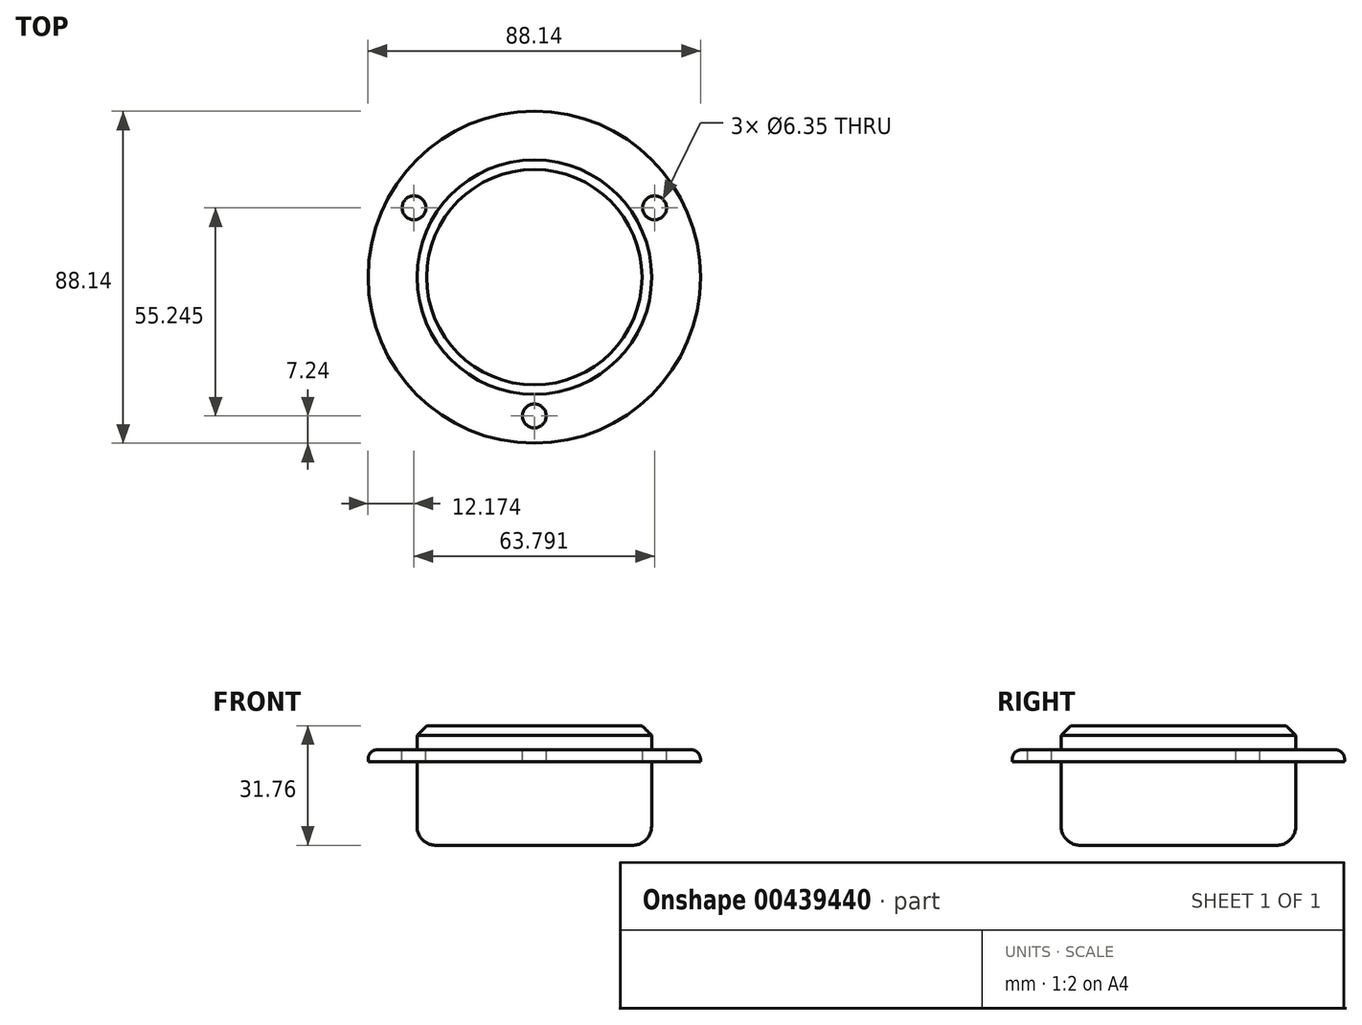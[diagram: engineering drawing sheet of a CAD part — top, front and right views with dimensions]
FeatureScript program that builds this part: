
annotation { "Feature Type Name" : "Feature", "Feature Type Description" : "" }
export const myFeature = defineFeature(function(context is Context, id is Id, definition is map)
    precondition{}
    {
        {
            var Q0;
            Q0=qCreatedBy(makeId("Top.planeOp"),FACE);
            var sketch = newSketch(context, id + "F0", { "sketchPlane" : qUnion([Q0])});
            skCircle(sketch, "E0", {"center": v(0, 0) * mm, "radius": 31.12 * mm});
            skCircle(sketch, "E1", {"center": v(0, 0) * mm, "radius": 44.07 * mm});
            skSolve(sketch);
        }
        {
            var Q0;
            Q0=makeQuery(id+"F0.imprint","IMPRINT",FACE,{"disambiguationData":[TD([[makeQuery(id+"F0.imprint","IMPRINT",EDGE,{"derivedFrom":sQuery(id+"F0.wireOp",EDGE,"E0")}),-1.0]])]});
            extrude(context, id + "F1", {"entities" : qUnion([Q0]), "depth" : 3.17 * mm, "offsetDistance" : 25.4 * mm});
        }
        {
            var Q0;
            Q0=makeQuery(id+"F1.opExtrude","CAP_EDGE",EDGE,{"disambiguationData":[OSD([sQuery(id+"F0.wireOp",EDGE,"E1")])],"isStart":false});
            fillet(context, id + "F2", {"entities" : qUnion([Q0]), "radius" : 2.54 * mm, "tangentPropagation" : true, "allowEdgeOverflow" : false});
        }
        {
            var Q0;
            Q0=makeQuery(id+"F1.opExtrude","CAP_FACE",FACE,{"disambiguationData":[OSD([sQuery(id+"F0.wireOp",EDGE,"E0"),sQuery(id+"F0.wireOp",EDGE,"E1")])],"isStart":false});
            var sketch = newSketch(context, id + "F3", { "sketchPlane" : qUnion([Q0])});
            skLineSegment(sketch, "E2", {"start": v(0, 0) * mm, "end": v(0, -36.83) * mm});
            skCircle(sketch, "E3", {"center": v(0, -36.83) * mm, "radius": 3.18 * mm});
            skCircle(sketch, "E4.1.0", {"center": v(31.9, 18.41) * mm, "radius": 3.18 * mm});
            skCircle(sketch, "E4.2.0", {"center": v(-31.9, 18.42) * mm, "radius": 3.18 * mm});
            skPoint(sketch, "E4.center", {"position": v(0, 0) * mm});
            skSolve(sketch);
        }
        {
            var Q0;
            Q0=makeQuery(id+"F3.imprint","IMPRINT",FACE,{"disambiguationData":[TD([[makeQuery(id+"F3.imprint","IMPRINT",EDGE,{"derivedFrom":sQuery(id+"F3.wireOp",EDGE,"E4.2.0")}),1.0]])]});
            var Q1;
            Q1=makeQuery(id+"F3.imprint","IMPRINT",FACE,{"disambiguationData":[TD([[makeQuery(id+"F3.imprint","IMPRINT",EDGE,{"derivedFrom":sQuery(id+"F3.wireOp",EDGE,"E4.1.0")}),1.0]])]});
            var Q2;
            Q2=makeQuery(id+"F3.imprint","IMPRINT",FACE,{"disambiguationData":[TD([[makeQuery(id+"F3.imprint","IMPRINT",EDGE,{"derivedFrom":sQuery(id+"F3.wireOp",EDGE,"E3")}),1.0]])]});
            extrude(context, id + "F4", {"entities" : qUnion([Q0, Q1, Q2]), "operationType" : NewBodyOperationType.REMOVE, "oppositeDirection" : true, "depth" : 25.4 * mm, "offsetDistance" : 25.4 * mm});
        }
        {
            var Q0;
            Q0=makeQuery(id+"F1.opExtrude","CAP_FACE",FACE,{"disambiguationData":[OSD([sQuery(id+"F0.wireOp",EDGE,"E0"),sQuery(id+"F0.wireOp",EDGE,"E1")])],"isStart":false});
            var sketch = newSketch(context, id + "F5", { "sketchPlane" : qUnion([Q0])});
            skCircle(sketch, "E5", {"center": v(0, 0) * mm, "radius": 31.12 * mm});
            skSolve(sketch);
        }
        {
            var Q0;
            Q0=makeQuery(id+"F5.imprint","IMPRINT",FACE,{"disambiguationData":[TD([[makeQuery(id+"F5.imprint","IMPRINT",EDGE,{"derivedFrom":sQuery(id+"F5.wireOp",EDGE,"E5")}),1.0]])]});
            extrude(context, id + "F6", {"entities" : qUnion([Q0]), "oppositeDirection" : true, "depth" : 25.4 * mm, "offsetDistance" : 25.4 * mm});
        }
        {
            var Q0;
            Q0=makeQuery(id+"F6.opExtrude","CAP_FACE",FACE,{"disambiguationData":[OSD([sQuery(id+"F5.wireOp",EDGE,"E5")])],"isStart":false});
            fillet(context, id + "F7", {"entities" : qUnion([Q0]), "radius" : 5.08 * mm, "tangentPropagation" : true, "allowEdgeOverflow" : false});
        }
        {
            var Q0;
            Q0=makeQuery(id+"F6.opExtrude","CAP_FACE",FACE,{"disambiguationData":[OSD([sQuery(id+"F5.wireOp",EDGE,"E5")])],"isStart":true});
            extrude(context, id + "F8", {"entities" : qUnion([Q0]), "operationType" : NewBodyOperationType.ADD, "depth" : 6.35 * mm, "offsetDistance" : 25.4 * mm});
        }
        {
            var Q0;
            Q0=makeQuery(id+"F8.opExtrude","CAP_FACE",FACE,{"disambiguationData":[OSD([sQuery(id+"F5.wireOp",EDGE,"E5")])],"isStart":false});
            chamfer(context, id + "F9", {"entities" : qUnion([Q0]), "width" : 2.54 * mm, "tangentPropagation" : true});
        }
    });
